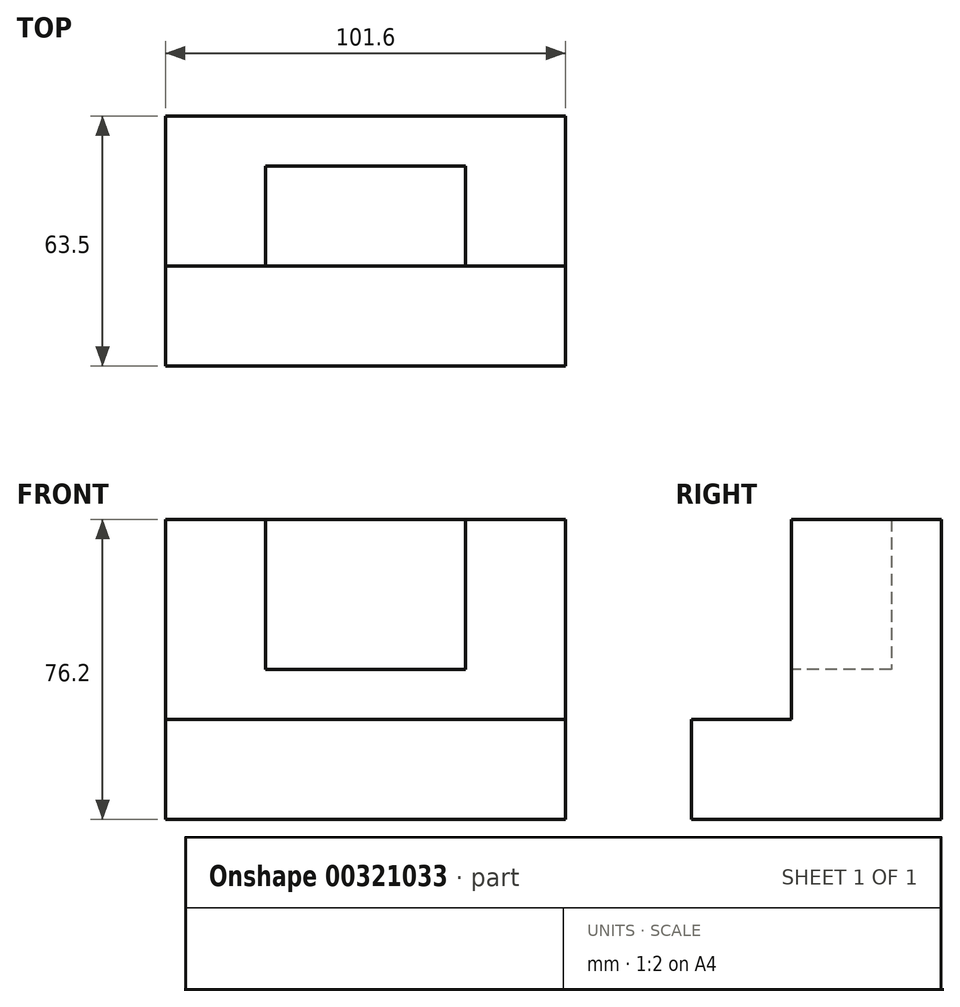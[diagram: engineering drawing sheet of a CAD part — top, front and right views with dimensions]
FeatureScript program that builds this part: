
annotation { "Feature Type Name" : "Feature", "Feature Type Description" : "" }
export const myFeature = defineFeature(function(context is Context, id is Id, definition is map)
    precondition{}
    {
        {
            var Q0;
            Q0=qCreatedBy(makeId("Right.planeOp"),FACE);
            var sketch = newSketch(context, id + "F0", { "sketchPlane" : qUnion([Q0])});
            skLineSegment(sketch, "E0", {"start": v(-48.22, -36.67) * mm, "end": v(15.28, -36.67) * mm});
            skLineSegment(sketch, "E1", {"start": v(15.28, -36.67) * mm, "end": v(15.28, 39.53) * mm});
            skLineSegment(sketch, "E2", {"start": v(15.28, 39.53) * mm, "end": v(-22.82, 39.53) * mm});
            skLineSegment(sketch, "E3", {"start": v(-22.82, 39.53) * mm, "end": v(-22.82, -11.27) * mm});
            skLineSegment(sketch, "E4", {"start": v(-22.82, -11.27) * mm, "end": v(-48.22, -11.27) * mm});
            skLineSegment(sketch, "E5", {"start": v(-48.22, -11.27) * mm, "end": v(-48.22, -36.67) * mm});
            skSolve(sketch);
        }
        {
            var Q0;
            Q0=makeQuery(id+"F0.imprint","IMPRINT",FACE,{"disambiguationData":[TD([[makeQuery(id+"F0.imprint","IMPRINT",EDGE,{"derivedFrom":sQuery(id+"F0.wireOp",EDGE,"E0")}),1.0]])]});
            extrude(context, id + "F1", {"entities" : qUnion([Q0]), "depth" : 101.6 * mm});
        }
        {
            var Q0;
            Q0=makeQuery(id+"F1.opExtrude","SWEPT_FACE",FACE,{"disambiguationData":[OSD([sQuery(id+"F0.wireOp",EDGE,"E3")])]});
            var sketch = newSketch(context, id + "F2", { "sketchPlane" : qUnion([Q0])});
            skLineSegment(sketch, "E6", {"start": v(25.4, 39.53) * mm, "end": v(25.4, 1.43) * mm});
            skLineSegment(sketch, "E7", {"start": v(25.4, 1.43) * mm, "end": v(76.2, 1.43) * mm});
            skLineSegment(sketch, "E8", {"start": v(76.2, 39.53) * mm, "end": v(76.2, 1.43) * mm});
            skSolve(sketch);
        }
        {
            var Q0;
            Q0 = qSketchRegion(id + "F2", true);
            var Q1;
            {var subQ0=sQuery(id+"F2.wireOp",EDGE,"E6");Q1=makeQuery(id+"F2.imprint","IMPRINT",FACE,{"disambiguationData":[TD([[makeQuery(id+"F2.imprint","IMPRINT",EDGE,{"derivedFrom":subQ0}),1.0]])]});}
            extrude(context, id + "F3", {"entities" : qUnion([Q0, Q1]), "operationType" : NewBodyOperationType.REMOVE, "oppositeDirection" : true, "depth" : 25.4 * mm});
        }
    });
